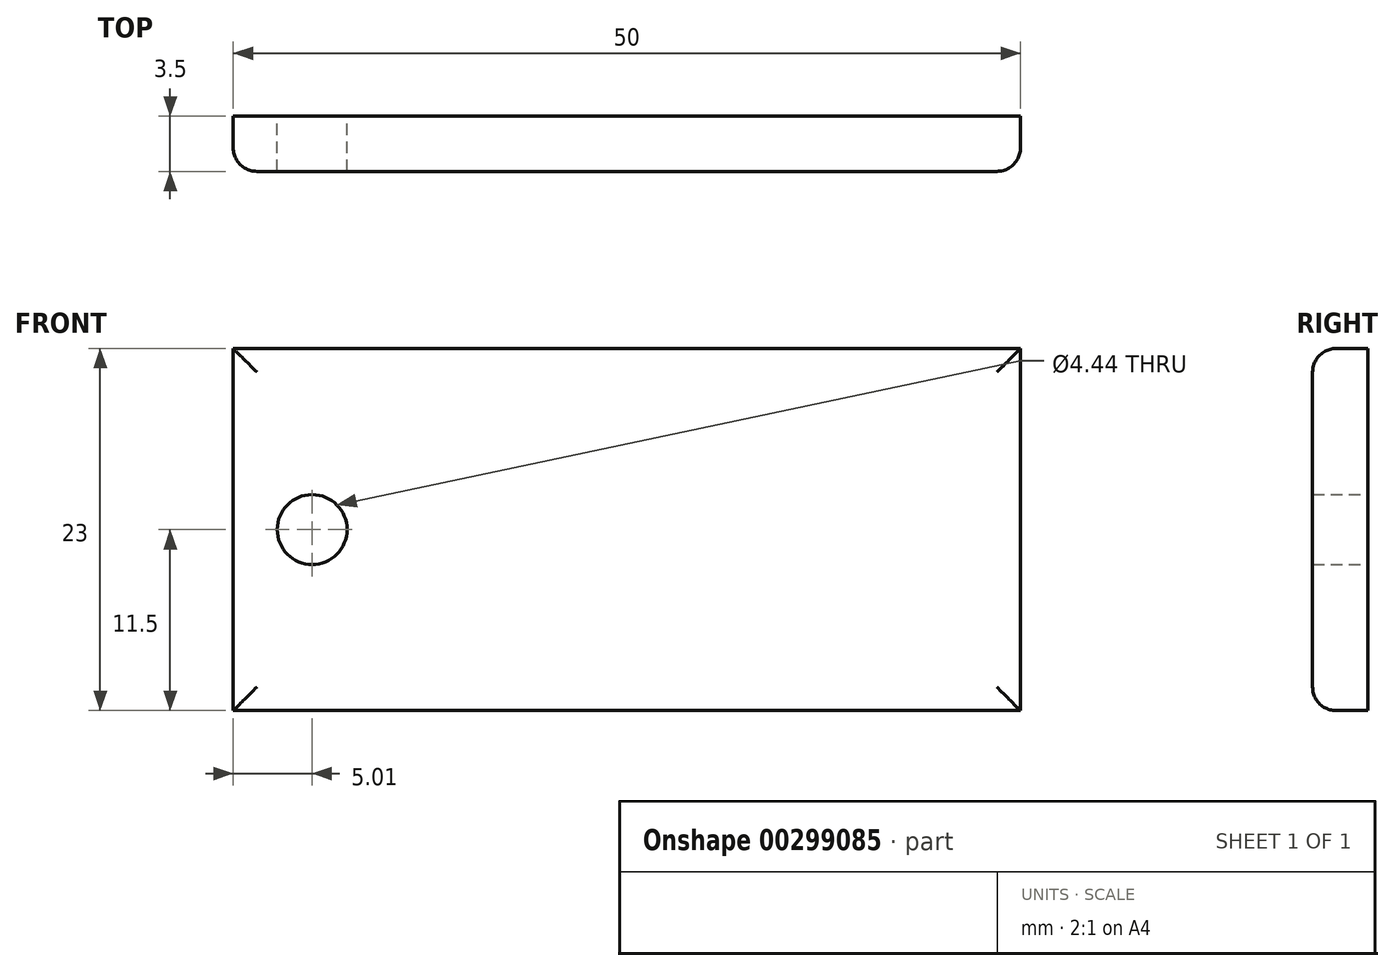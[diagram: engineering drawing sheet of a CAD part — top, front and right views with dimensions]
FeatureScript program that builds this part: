
annotation { "Feature Type Name" : "Feature", "Feature Type Description" : "" }
export const myFeature = defineFeature(function(context is Context, id is Id, definition is map)
    precondition{}
    {
        {
            var Q0;
            Q0=qCreatedBy(makeId("Front.planeOp"),FACE);
            var sketch = newSketch(context, id + "F0", { "sketchPlane" : qUnion([Q0])});
            skLineSegment(sketch, "E0.bottom", {"start": v(25, -11.5) * mm, "end": v(-25, -11.5) * mm});
            skLineSegment(sketch, "E0.top", {"start": v(25, 11.5) * mm, "end": v(-25, 11.5) * mm});
            skLineSegment(sketch, "E0.left", {"start": v(25, -11.5) * mm, "end": v(25, 11.5) * mm});
            skLineSegment(sketch, "E0.right", {"start": v(-25, -11.5) * mm, "end": v(-25, 11.5) * mm});
            skPoint(sketch, "E0.middle", {"position": v(0, 0) * mm});
            skPoint(sketch, "E1", {"position": v(-25, 0) * mm});
            skCircle(sketch, "E2", {"center": v(-19.99, 0) * mm, "radius": 2.22 * mm});
            skSolve(sketch);
        }
        {
            var Q0;
            Q0=qSketchRegion(id+"F0",true);
            extrude(context, id + "F1", {"entities" : qUnion([Q0]), "depth" : 3.5 * mm});
        }
        {
            var Q0;
            Q0=makeQuery(id+"F1.opExtrude","CAP_EDGE",EDGE,{"disambiguationData":[OSD([sQuery(id+"F0.wireOp",EDGE,"E0.bottom")])],"isStart":false});
            var Q1;
            Q1=makeQuery(id+"F1.opExtrude","CAP_EDGE",EDGE,{"disambiguationData":[OSD([sQuery(id+"F0.wireOp",EDGE,"E0.right")])],"isStart":false});
            var Q2;
            Q2=makeQuery(id+"F1.opExtrude","CAP_EDGE",EDGE,{"disambiguationData":[OSD([sQuery(id+"F0.wireOp",EDGE,"E0.left")])],"isStart":false});
            var Q3;
            Q3=makeQuery(id+"F1.opExtrude","CAP_EDGE",EDGE,{"disambiguationData":[OSD([sQuery(id+"F0.wireOp",EDGE,"E0.top")])],"isStart":false});
            fillet(context, id + "F2", {"entities" : qUnion([Q0, Q1, Q2, Q3]), "radius" : 1.5 * mm, "tangentPropagation" : true, "allowEdgeOverflow" : false});
        }
    });
